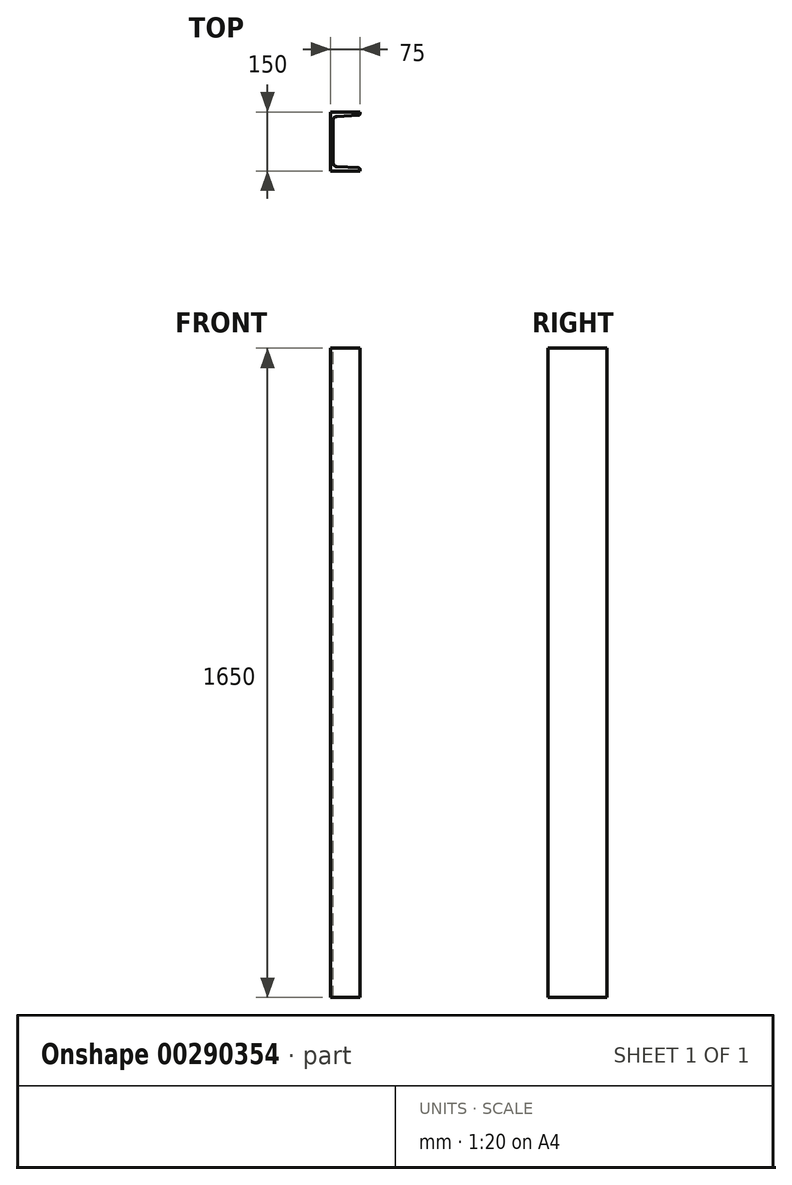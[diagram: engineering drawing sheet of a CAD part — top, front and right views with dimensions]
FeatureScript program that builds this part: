
annotation { "Feature Type Name" : "Feature", "Feature Type Description" : "" }
export const myFeature = defineFeature(function(context is Context, id is Id, definition is map)
    precondition{}
    {
        {
            var Q0;
            Q0=qCreatedBy(makeId("Top.planeOp"),FACE);
            var sketch = newSketch(context, id + "F0", { "sketchPlane" : qUnion([Q0])});
            skLineSegment(sketch, "E0", {"start": v(-184.9, -150) * mm, "end": v(-184.9, 0) * mm});
            skLineSegment(sketch, "E1", {"start": v(-184.9, 0) * mm, "end": v(-109.9, 0) * mm});
            skLineSegment(sketch, "E2", {"start": v(-109.9, 0) * mm, "end": v(-109.9, -3.29) * mm});
            skLineSegment(sketch, "E3", {"start": v(-178.4, -21.11) * mm, "end": v(-178.4, -128.89) * mm});
            skLineSegment(sketch, "E4", {"start": v(-109.9, -150) * mm, "end": v(-184.9, -150) * mm});
            skPoint(sketch, "E5", {"position": v(-147.4, -10) * mm});
            skLineSegment(sketch, "E6", {"start": v(-168.93, -11.13) * mm, "end": v(-114.64, -8.28) * mm});
            skArc(sketch, "E7.filletArc", {"start": v(-168.93, -11.13) * mm, "mid": v(-175.66, -14.23) * mm, "end": v(-178.4, -21.11) * mm});
            skPoint(sketch, "E8.visualSharp", {"position": v(-109.9, -8.03) * mm});
            skArc(sketch, "E8.filletArc", {"start": v(-114.64, -8.28) * mm, "mid": v(-111.28, -6.73) * mm, "end": v(-109.9, -3.29) * mm});
            skPoint(sketch, "E9.endSnap0", {"position": v(-184.9, -75) * mm});
            skLineSegment(sketch, "E10.MirrorCS", {"start": v(-109.9, -150) * mm, "end": v(-109.9, -146.71) * mm});
            skArc(sketch, "E11.MirrorCS", {"start": v(-114.64, -141.72) * mm, "mid": v(-111.28, -143.27) * mm, "end": v(-109.9, -146.71) * mm});
            skArc(sketch, "E12.MirrorCS", {"start": v(-168.93, -138.87) * mm, "mid": v(-175.66, -135.77) * mm, "end": v(-178.4, -128.89) * mm});
            skLineSegment(sketch, "E13.MirrorCS", {"start": v(-168.93, -138.87) * mm, "end": v(-114.64, -141.72) * mm});
            skPoint(sketch, "E14.MirrorP", {"position": v(-109.9, -141.97) * mm});
            skPoint(sketch, "E15.MirrorP", {"position": v(-147.4, -140) * mm});
            skPoint(sketch, "E9.start.orphan", {"position": v(-184.9, -75) * mm});
            skSolve(sketch);
        }
        {
            var Q0;
            Q0=makeQuery(id+"F0.imprint","IMPRINT",FACE,{"disambiguationData":[TD([[makeQuery(id+"F0.imprint","IMPRINT",EDGE,{"derivedFrom":sQuery(id+"F0.wireOp",EDGE,"E0")}),-1.0]])]});
            extrude(context, id + "F1", {"entities" : qUnion([Q0]), "oppositeDirection" : true, "depth" : 1650 * mm});
        }
    });
